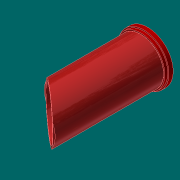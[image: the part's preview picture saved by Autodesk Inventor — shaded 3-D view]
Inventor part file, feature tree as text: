
AUTODESK INVENTOR PART (.ipt)
format: ipt  version: 2017.3 (Build 213257000, 257)  size: 139,776 bytes
history: native  units: in
note: dims shown in document units (in); Inventor stores cm internally (conversion verified against a paired STEP export)
features: other x3, extrude x2, sketch x2
ambient origin geometry x8: Origin, YZ Plane, XZ Plane, XY Plane, X Axis, Y Axis, Z Axis, Center Point
bodies: Solid1 (feature_tree)
feature tree (7):
  other  "A1-19010-100-02 HCWI nozzle insert.ipt"
  extrude  "Extrusion1"  Depth=0.5in
  extrude  "Extrusion2"  Depth=0.5in TaperAngle=0.0deg
  other  "Solid1::A1-19010-100-02 HCWI nozzle insert.ipt"
  other  "TaggingFeature1"
  sketch  "Sketch2"  dims[d0=0.3937in]
  sketch  "Sketch3"  dims[d1=2.0in d2=0.0in d3=28.52in d4=3.75in d5=0.0in d6=27.5in d7=68.7402in d8=0.0in d9=25.0in d12=0.0in d13=0.0312in d16=0.0312in d17=0.0312in d18=0.2749in d20=0.0in d24=0.25in d10=30.5118in d11=0.5in d14=2.0in d15=0.0in d19=0.0in d21=29.0157in d22=0.5in d23=0.0in]
